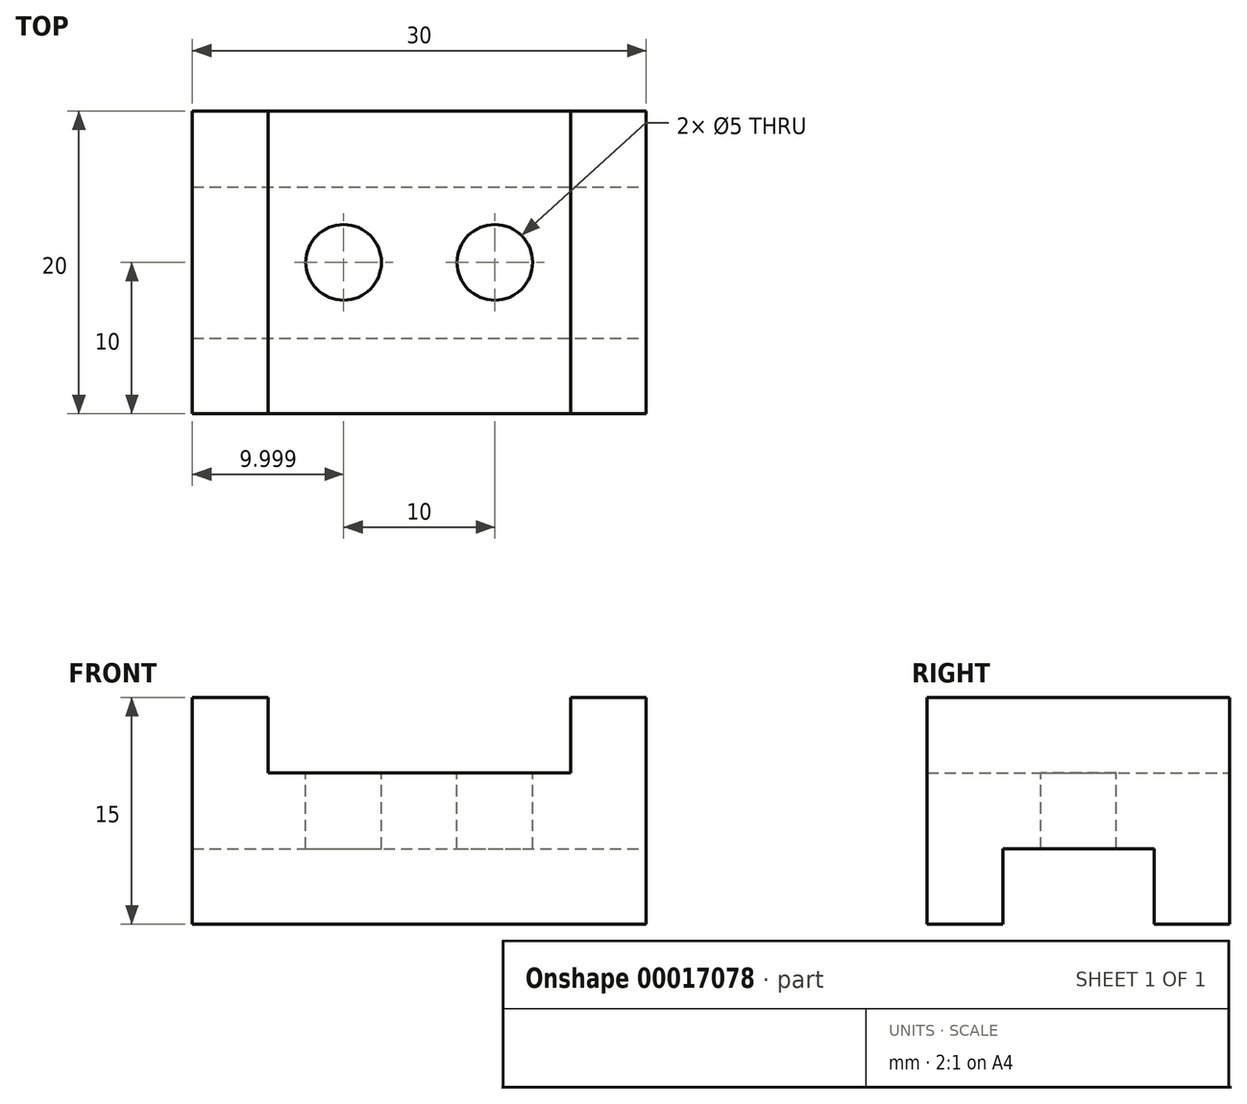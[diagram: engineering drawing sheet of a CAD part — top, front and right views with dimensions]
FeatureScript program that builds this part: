
annotation { "Feature Type Name" : "Feature", "Feature Type Description" : "" }
export const myFeature = defineFeature(function(context is Context, id is Id, definition is map)
    precondition{}
    {
        {
            var Q0;
            Q0=qCreatedBy(makeId("Front.planeOp"),FACE);
            var sketch = newSketch(context, id + "F0", { "sketchPlane" : qUnion([Q0])});
            skLineSegment(sketch, "E0", {"start": v(-28.74, 12.64) * mm, "end": v(-23.74, 12.64) * mm});
            skLineSegment(sketch, "E1", {"start": v(-23.74, 12.64) * mm, "end": v(-23.74, 7.64) * mm});
            skLineSegment(sketch, "E2", {"start": v(-23.74, 7.64) * mm, "end": v(-3.74, 7.64) * mm});
            skLineSegment(sketch, "E3", {"start": v(-3.74, 7.64) * mm, "end": v(-3.74, 12.64) * mm});
            skLineSegment(sketch, "E4", {"start": v(-3.74, 12.64) * mm, "end": v(1.26, 12.64) * mm});
            skLineSegment(sketch, "E5", {"start": v(1.26, 12.64) * mm, "end": v(1.26, -2.36) * mm});
            skLineSegment(sketch, "E6", {"start": v(1.26, -2.36) * mm, "end": v(-28.74, -2.36) * mm});
            skLineSegment(sketch, "E7", {"start": v(-28.74, -2.36) * mm, "end": v(-28.74, 12.64) * mm});
            skSolve(sketch);
        }
        {
            var Q0;
            Q0=makeQuery(id+"F0.imprint","IMPRINT",FACE,{"disambiguationData":[TD([[makeQuery(id+"F0.imprint","IMPRINT",EDGE,{"derivedFrom":sQuery(id+"F0.wireOp",EDGE,"E0")}),-1.0]])]});
            extrude(context, id + "F1", {"entities" : qUnion([Q0]), "depth" : 20 * mm});
        }
        {
            var Q0;
            Q0=makeQuery(id+"F1.opExtrude","SWEPT_FACE",FACE,{"disambiguationData":[OSD([sQuery(id+"F0.wireOp",EDGE,"E5")])]});
            var sketch = newSketch(context, id + "F2", { "sketchPlane" : qUnion([Q0])});
            skPoint(sketch, "E8", {"position": v(-15, -2.36) * mm});
            skPoint(sketch, "E9", {"position": v(-5, -2.36) * mm});
            skLineSegment(sketch, "E10.bottom", {"start": v(-15, -2.36) * mm, "end": v(-5, -2.36) * mm});
            skLineSegment(sketch, "E10.top", {"start": v(-15, 2.64) * mm, "end": v(-5, 2.64) * mm});
            skLineSegment(sketch, "E10.left", {"start": v(-15, -2.36) * mm, "end": v(-15, 2.64) * mm});
            skLineSegment(sketch, "E10.right", {"start": v(-5, -2.36) * mm, "end": v(-5, 2.64) * mm});
            skSolve(sketch);
        }
        {
            var Q0;
            Q0=makeQuery(id+"F2.imprint","IMPRINT",FACE,{"disambiguationData":[TD([[makeQuery(id+"F2.imprint","IMPRINT",EDGE,{"derivedFrom":sQuery(id+"F2.wireOp",EDGE,"E10.bottom")}),1.0]])]});
            extrude(context, id + "F3", {"entities" : qUnion([Q0]), "operationType" : NewBodyOperationType.REMOVE, "endBound" : BoundingType.THROUGH_ALL, "oppositeDirection" : true, "depth" : 25 * mm});
        }
        {
            var Q0;
            Q0=makeQuery(id+"F1.opExtrude","SWEPT_FACE",FACE,{"disambiguationData":[OSD([sQuery(id+"F0.wireOp",EDGE,"E2")])]});
            var sketch = newSketch(context, id + "F4", { "sketchPlane" : qUnion([Q0])});
            skCircle(sketch, "E11", {"center": v(-18.74, -10) * mm, "radius": 2.5 * mm});
            skCircle(sketch, "E12", {"center": v(-8.74, -10) * mm, "radius": 2.5 * mm});
            skSolve(sketch);
        }
        {
            var Q0;
            Q0=makeQuery(id+"F4.imprint","IMPRINT",FACE,{"disambiguationData":[TD([[makeQuery(id+"F4.imprint","IMPRINT",EDGE,{"derivedFrom":sQuery(id+"F4.wireOp",EDGE,"E11")}),1.0]])]});
            var Q1;
            Q1=makeQuery(id+"F4.imprint","IMPRINT",FACE,{"disambiguationData":[TD([[makeQuery(id+"F4.imprint","IMPRINT",EDGE,{"derivedFrom":sQuery(id+"F4.wireOp",EDGE,"E12")}),1.0]])]});
            extrude(context, id + "F5", {"entities" : qUnion([Q0, Q1]), "operationType" : NewBodyOperationType.REMOVE, "endBound" : BoundingType.THROUGH_ALL, "oppositeDirection" : true, "depth" : 25 * mm});
        }
    });
